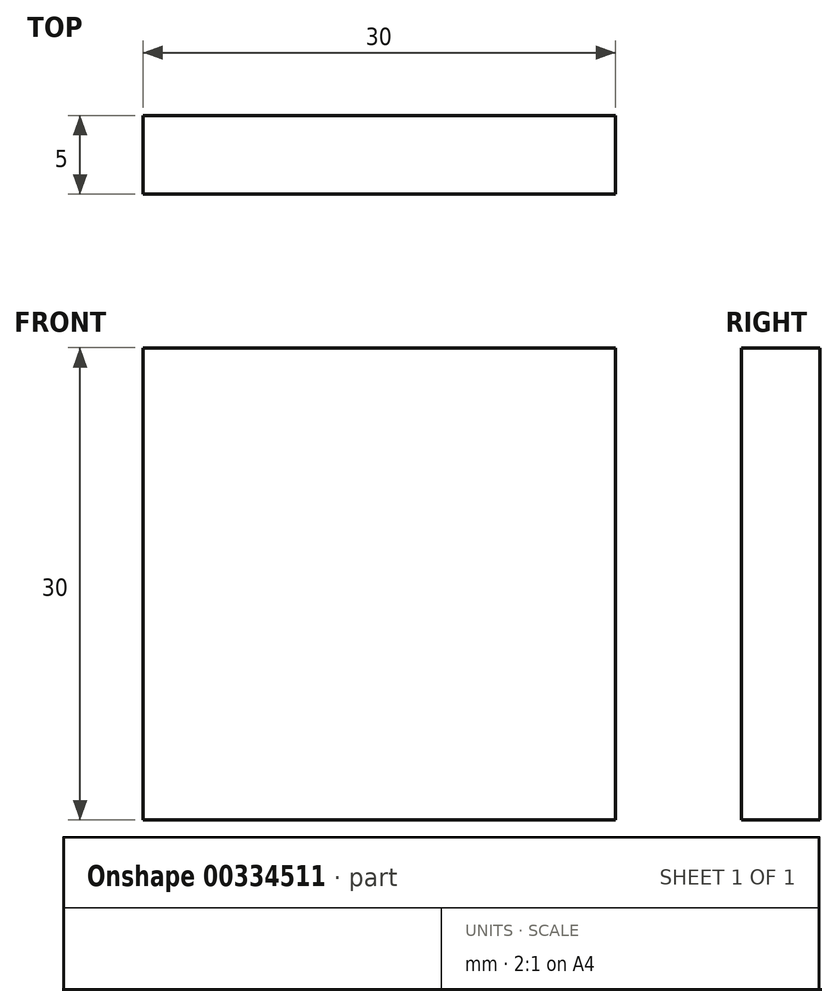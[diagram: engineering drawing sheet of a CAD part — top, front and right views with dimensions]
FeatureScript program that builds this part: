
annotation { "Feature Type Name" : "Feature", "Feature Type Description" : "" }
export const myFeature = defineFeature(function(context is Context, id is Id, definition is map)
    precondition{}
    {
        {
            var Q0;
            Q0=qCreatedBy(makeId("Front.planeOp"),FACE);
            var sketch = newSketch(context, id + "F0", { "sketchPlane" : qUnion([Q0])});
            skLineSegment(sketch, "E0.bottom", {"start": v(-12.55, 12.04) * mm, "end": v(17.45, 12.04) * mm});
            skLineSegment(sketch, "E0.top", {"start": v(-12.55, -17.96) * mm, "end": v(17.45, -17.96) * mm});
            skLineSegment(sketch, "E0.left", {"start": v(-12.55, 12.04) * mm, "end": v(-12.55, -17.96) * mm});
            skLineSegment(sketch, "E0.right", {"start": v(17.45, 12.04) * mm, "end": v(17.45, -17.96) * mm});
            skSolve(sketch);
        }
        {
            var Q0;
            Q0 = qSketchRegion(id + "F0", true);
            extrude(context, id + "F1", {"entities" : qUnion([Q0]), "depth" : 5 * mm});
        }
    });
